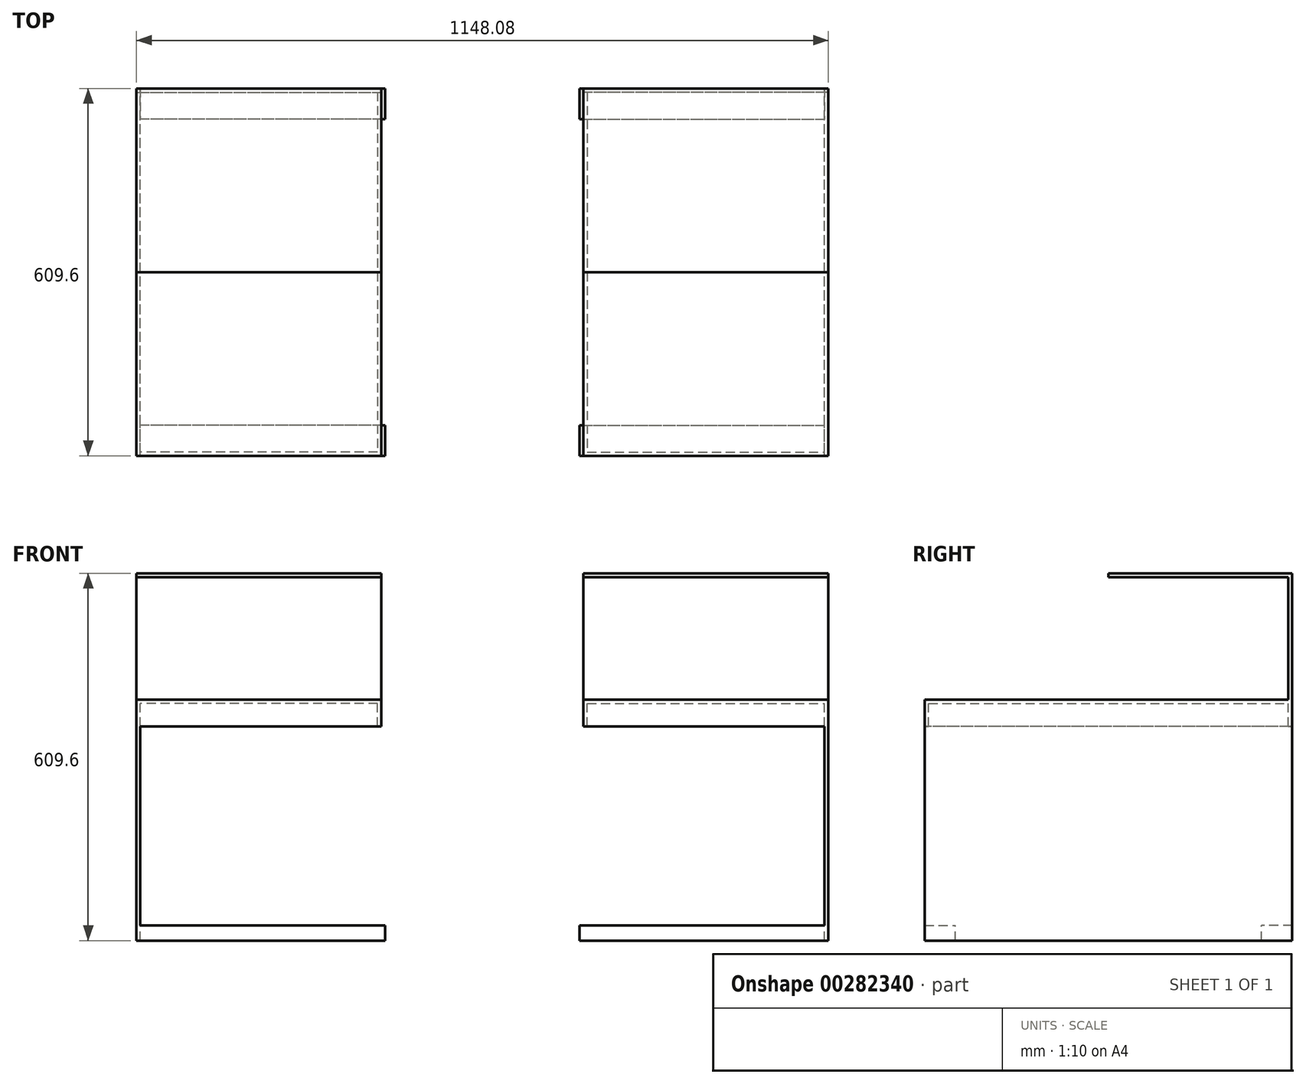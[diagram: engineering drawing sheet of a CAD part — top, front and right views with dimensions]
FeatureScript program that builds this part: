
annotation { "Feature Type Name" : "Feature", "Feature Type Description" : "" }
export const myFeature = defineFeature(function(context is Context, id is Id, definition is map)
    precondition{}
    {
        {
            var Q0;
            Q0=qCreatedBy(makeId("Top.planeOp"),FACE);
            var sketch = newSketch(context, id + "F0", { "sketchPlane" : qUnion([Q0])});
            skLineSegment(sketch, "E0.bottom", {"start": v(203.2, 304.8) * mm, "end": v(-203.2, 304.8) * mm});
            skLineSegment(sketch, "E0.top", {"start": v(203.2, -304.8) * mm, "end": v(-203.2, -304.8) * mm});
            skLineSegment(sketch, "E0.left", {"start": v(203.2, 304.8) * mm, "end": v(203.2, -304.8) * mm});
            skLineSegment(sketch, "E0.right", {"start": v(-203.2, 304.8) * mm, "end": v(-203.2, -304.8) * mm});
            skPoint(sketch, "E0.middle", {"position": v(0, 0) * mm});
            skSolve(sketch);
        }
        {
            var Q0;
            Q0=makeQuery(id+"F0.imprint","IMPRINT",FACE,{"disambiguationData":[TD([[makeQuery(id+"F0.imprint","IMPRINT",EDGE,{"derivedFrom":sQuery(id+"F0.wireOp",EDGE,"E0.bottom")}),1.0]])]});
            extrude(context, id + "F1", {"entities" : qUnion([Q0]), "depth" : 6.35 * mm});
        }
        {
            var Q0;
            Q0=makeQuery(id+"F1.opExtrude","CAP_FACE",FACE,{"disambiguationData":[OSD([sQuery(id+"F0.wireOp",EDGE,"E0.bottom"),sQuery(id+"F0.wireOp",EDGE,"E0.top"),sQuery(id+"F0.wireOp",EDGE,"E0.left"),sQuery(id+"F0.wireOp",EDGE,"E0.right")])],"isStart":true});
            var sketch = newSketch(context, id + "F2", { "sketchPlane" : qUnion([Q0])});
            skLineSegment(sketch, "E1.0", {"start": v(196.85, 298.45) * mm, "end": v(-196.85, 298.45) * mm});
            skLineSegment(sketch, "E1.1", {"start": v(196.85, -298.45) * mm, "end": v(196.85, 298.45) * mm});
            skLineSegment(sketch, "E1.2", {"start": v(-196.85, -298.45) * mm, "end": v(196.85, -298.45) * mm});
            skLineSegment(sketch, "E1.3", {"start": v(-196.85, 298.45) * mm, "end": v(-196.85, -298.45) * mm});
            skLineSegment(sketch, "E2.0.0", {"start": v(203.2, 304.8) * mm, "end": v(-203.2, 304.8) * mm});
            skLineSegment(sketch, "E2.0.1", {"start": v(-203.2, 304.8) * mm, "end": v(-203.2, -304.8) * mm});
            skLineSegment(sketch, "E2.0.2", {"start": v(-203.2, -304.8) * mm, "end": v(203.2, -304.8) * mm});
            skLineSegment(sketch, "E2.0.3", {"start": v(203.2, -304.8) * mm, "end": v(203.2, 304.8) * mm});
            skSolve(sketch);
        }
        {
            var Q0;
            Q0=makeQuery(id+"F2.imprint","IMPRINT",FACE,{"disambiguationData":[TD([[makeQuery(id+"F2.imprint","IMPRINT",EDGE,{"derivedFrom":sQuery(id+"F2.wireOp",EDGE,"E1.0")}),-1.0]])]});
            extrude(context, id + "F3", {"entities" : qUnion([Q0]), "operationType" : NewBodyOperationType.ADD, "depth" : 38.1 * mm});
        }
        {
            var Q0;
            Q0=makeQuery(id+"F3.opExtrude","CAP_FACE",FACE,{"disambiguationData":[OSD([sQuery(id+"F2.wireOp",EDGE,"E1.0"),sQuery(id+"F2.wireOp",EDGE,"E1.1"),sQuery(id+"F2.wireOp",EDGE,"E1.2"),sQuery(id+"F2.wireOp",EDGE,"E1.3"),sQuery(id+"F2.wireOp",EDGE,"E2.0.0"),sQuery(id+"F2.wireOp",EDGE,"E2.0.1"),sQuery(id+"F2.wireOp",EDGE,"E2.0.2"),sQuery(id+"F2.wireOp",EDGE,"E2.0.3")])],"isStart":false});
            var sketch = newSketch(context, id + "F4", { "sketchPlane" : qUnion([Q0])});
            skLineSegment(sketch, "E3.bottom", {"start": v(-203.2, 304.8) * mm, "end": v(-196.85, 304.8) * mm});
            skLineSegment(sketch, "E3.top", {"start": v(-203.2, -304.8) * mm, "end": v(-196.85, -304.8) * mm});
            skLineSegment(sketch, "E3.left", {"start": v(-203.2, 304.8) * mm, "end": v(-203.2, -304.8) * mm});
            skLineSegment(sketch, "E3.right", {"start": v(-196.85, 304.8) * mm, "end": v(-196.85, -304.8) * mm});
            skSolve(sketch);
        }
        {
            var Q0;
            Q0 = qSketchRegion(id + "F4", true);
            extrude(context, id + "F5", {"entities" : qUnion([Q0]), "operationType" : NewBodyOperationType.ADD, "depth" : 355.6 * mm});
        }
        {
            var Q0;
            Q0=makeQuery(id+"F1.opExtrude","CAP_FACE",FACE,{"disambiguationData":[OSD([sQuery(id+"F0.wireOp",EDGE,"E0.bottom"),sQuery(id+"F0.wireOp",EDGE,"E0.top"),sQuery(id+"F0.wireOp",EDGE,"E0.left"),sQuery(id+"F0.wireOp",EDGE,"E0.right")])],"isStart":false});
            var sketch = newSketch(context, id + "F6", { "sketchPlane" : qUnion([Q0])});
            skLineSegment(sketch, "E4.bottom", {"start": v(-203.2, 304.8) * mm, "end": v(203.2, 304.8) * mm});
            skLineSegment(sketch, "E4.top", {"start": v(-203.2, 298.45) * mm, "end": v(203.2, 298.45) * mm});
            skLineSegment(sketch, "E4.left", {"start": v(-203.2, 304.8) * mm, "end": v(-203.2, 298.45) * mm});
            skLineSegment(sketch, "E4.right", {"start": v(203.2, 304.8) * mm, "end": v(203.2, 298.45) * mm});
            skSolve(sketch);
        }
        {
            var Q0;
            Q0=makeQuery(id+"F6.imprint","IMPRINT",FACE,{"disambiguationData":[TD([[makeQuery(id+"F6.imprint","IMPRINT",EDGE,{"derivedFrom":sQuery(id+"F6.wireOp",EDGE,"E4.bottom")}),1.0]])]});
            extrude(context, id + "F7", {"entities" : qUnion([Q0]), "operationType" : NewBodyOperationType.ADD, "depth" : 203.2 * mm});
        }
        {
            var Q0;
            Q0=makeQuery(id+"F7.boolean.opBoolean","MERGE",FACE,{"derivedFrom":[makeQuery(id+"F5.boolean.opBoolean","MERGE",FACE,{"derivedFrom":[makeQuery(id+"F3.boolean.opBoolean","MERGE",FACE,{"derivedFrom":[makeQuery(id+"F1.opExtrude","SWEPT_FACE",FACE,{"disambiguationData":[OSD([sQuery(id+"F0.wireOp",EDGE,"E0.bottom")])]}),makeQuery(id+"F3.opExtrude","SWEPT_FACE",FACE,{"disambiguationData":[OSD([sQuery(id+"F2.wireOp",EDGE,"E2.0.2")])]})]}),makeQuery(id+"F5.opExtrude","SWEPT_FACE",FACE,{"disambiguationData":[OSD([sQuery(id+"F4.wireOp",EDGE,"E3.top")])]})]}),makeQuery(id+"F7.opExtrude","SWEPT_FACE",FACE,{"disambiguationData":[OSD([sQuery(id+"F6.wireOp",EDGE,"E4.bottom")])]})]});
            var sketch = newSketch(context, id + "F8", { "sketchPlane" : qUnion([Q0])});
            skLineSegment(sketch, "E5.bottom", {"start": v(-203.2, 209.55) * mm, "end": v(203.2, 209.55) * mm});
            skLineSegment(sketch, "E5.top", {"start": v(-203.2, 215.9) * mm, "end": v(203.2, 215.9) * mm});
            skLineSegment(sketch, "E5.left", {"start": v(-203.2, 209.55) * mm, "end": v(-203.2, 215.9) * mm});
            skLineSegment(sketch, "E5.right", {"start": v(203.2, 209.55) * mm, "end": v(203.2, 215.9) * mm});
            skSolve(sketch);
        }
        {
            var Q0;
            Q0=makeQuery(id+"F8.imprint","IMPRINT",FACE,{"disambiguationData":[TD([[makeQuery(id+"F8.imprint","IMPRINT",EDGE,{"derivedFrom":sQuery(id+"F8.wireOp",EDGE,"E5.bottom")}),1.0]])]});
            extrude(context, id + "F9", {"entities" : qUnion([Q0]), "operationType" : NewBodyOperationType.ADD, "oppositeDirection" : true, "depth" : 304.8 * mm});
        }
        {
            var Q0;
            Q0=makeQuery(id+"F5.boolean.opBoolean","MERGE",FACE,{"derivedFrom":[makeQuery(id+"F3.opExtrude","SWEPT_FACE",FACE,{"disambiguationData":[OSD([sQuery(id+"F2.wireOp",EDGE,"E1.3")])]}),makeQuery(id+"F5.opExtrude","SWEPT_FACE",FACE,{"disambiguationData":[OSD([sQuery(id+"F4.wireOp",EDGE,"E3.right")])]})]});
            var sketch = newSketch(context, id + "F10", { "sketchPlane" : qUnion([Q0])});
            skLineSegment(sketch, "E6.bottom", {"start": v(-304.8, -393.7) * mm, "end": v(-254, -393.7) * mm});
            skLineSegment(sketch, "E6.top", {"start": v(-304.8, -368.3) * mm, "end": v(-254, -368.3) * mm});
            skLineSegment(sketch, "E6.left", {"start": v(-304.8, -393.7) * mm, "end": v(-304.8, -368.3) * mm});
            skLineSegment(sketch, "E6.right", {"start": v(-254, -393.7) * mm, "end": v(-254, -368.3) * mm});
            skLineSegment(sketch, "E7.bottom", {"start": v(304.8, -393.7) * mm, "end": v(254, -393.7) * mm});
            skLineSegment(sketch, "E7.top", {"start": v(304.8, -368.3) * mm, "end": v(254, -368.3) * mm});
            skLineSegment(sketch, "E7.left", {"start": v(304.8, -393.7) * mm, "end": v(304.8, -368.3) * mm});
            skLineSegment(sketch, "E7.right", {"start": v(254, -393.7) * mm, "end": v(254, -368.3) * mm});
            skSolve(sketch);
        }
        {
            var Q0;
            Q0=makeQuery(id+"F10.imprint","IMPRINT",FACE,{"disambiguationData":[TD([[makeQuery(id+"F10.imprint","IMPRINT",EDGE,{"derivedFrom":sQuery(id+"F10.wireOp",EDGE,"E6.bottom")}),1.0]])]});
            var Q1;
            Q1=makeQuery(id+"F10.imprint","IMPRINT",FACE,{"disambiguationData":[TD([[makeQuery(id+"F10.imprint","IMPRINT",EDGE,{"derivedFrom":sQuery(id+"F10.wireOp",EDGE,"E7.bottom")}),1.0]])]});
            extrude(context, id + "F11", {"entities" : qUnion([Q0, Q1]), "operationType" : NewBodyOperationType.ADD, "depth" : 406.4 * mm});
        }
        {
            var Q0;
            Q0=makeQuery(id+"F9.boolean.opBoolean","MERGE",FACE,{"derivedFrom":[makeQuery(id+"F7.boolean.opBoolean","MERGE",FACE,{"derivedFrom":[makeQuery(id+"F3.boolean.opBoolean","MERGE",FACE,{"derivedFrom":[makeQuery(id+"F1.opExtrude","SWEPT_FACE",FACE,{"disambiguationData":[OSD([sQuery(id+"F0.wireOp",EDGE,"E0.left")])]}),makeQuery(id+"F3.opExtrude","SWEPT_FACE",FACE,{"disambiguationData":[OSD([sQuery(id+"F2.wireOp",EDGE,"E2.0.3")])]})]}),makeQuery(id+"F7.opExtrude","SWEPT_FACE",FACE,{"disambiguationData":[OSD([sQuery(id+"F6.wireOp",EDGE,"E4.right")])]})]}),makeQuery(id+"F9.opExtrude","SWEPT_FACE",FACE,{"disambiguationData":[OSD([sQuery(id+"F8.wireOp",EDGE,"E5.left")])]})]});
            cPlane(context, id + "F12", {"entities" : qUnion([Q0]), "cplaneType" : CPlaneType.OFFSET, "offset" : 167.64 * mm, "width" : 152.4 * mm, "height" : 152.4 * mm});
        }
        {
            var Q0;
            Q0=makeQuery(id+"F1.opExtrude","SWEPT_BODY",BODY,{"disambiguationData":[OSD([sQuery(id+"F0.wireOp",EDGE,"E0.bottom"),sQuery(id+"F0.wireOp",EDGE,"E0.top"),sQuery(id+"F0.wireOp",EDGE,"E0.left"),sQuery(id+"F0.wireOp",EDGE,"E0.right")])]});
            var Q1;
            Q1=qCreatedBy(id+"F12.planeOp",FACE);
            mirror(context, id + "F13", {"entities" : qUnion([Q0]), "mirrorPlane" : qUnion([Q1])});
        }
    });
